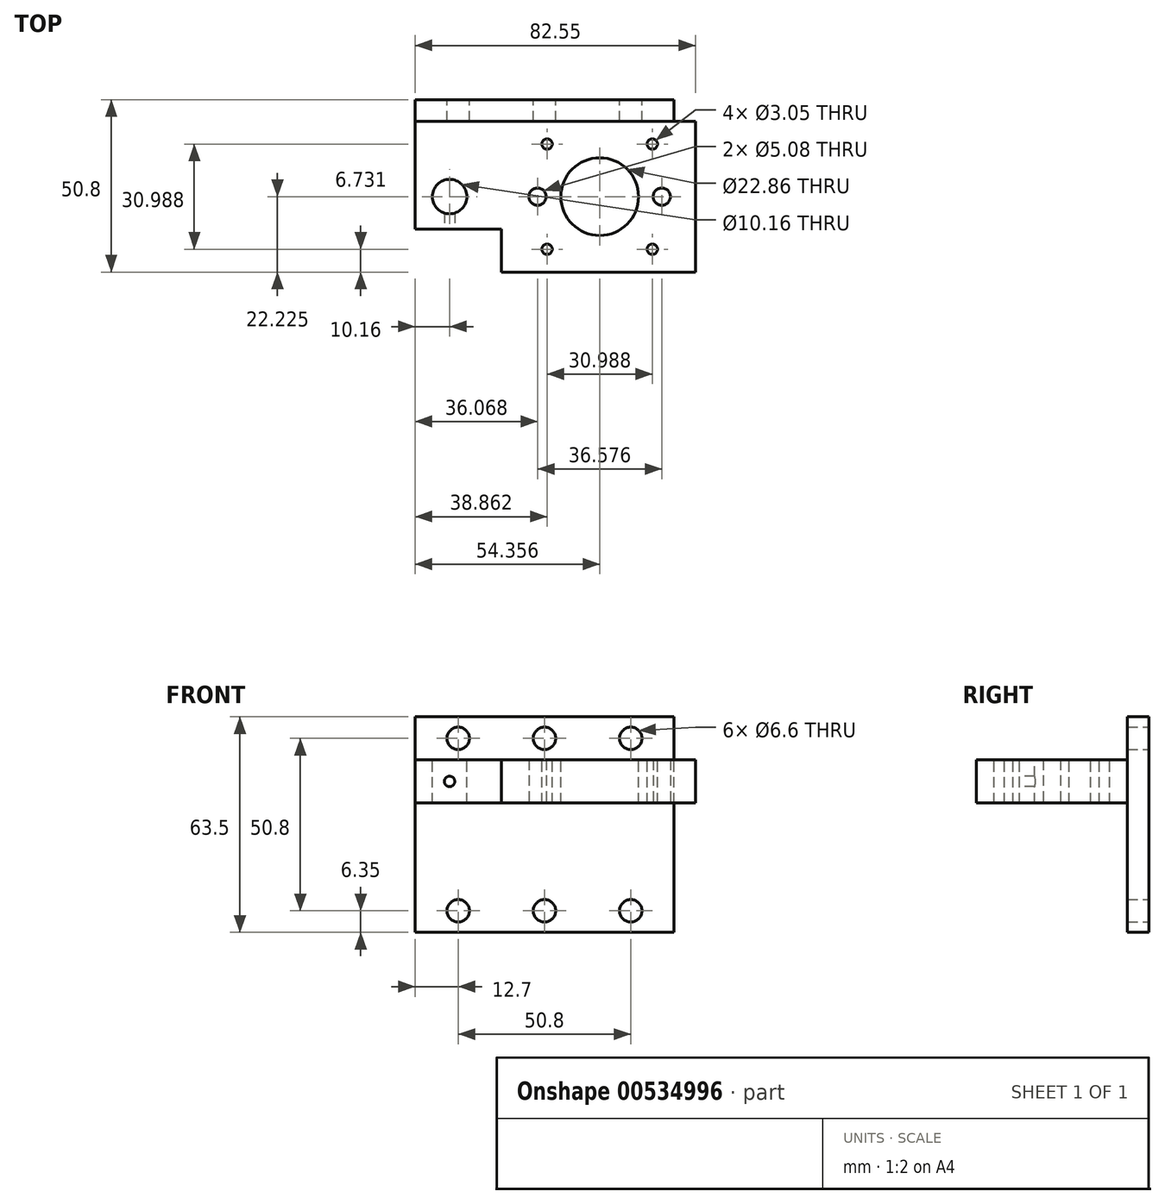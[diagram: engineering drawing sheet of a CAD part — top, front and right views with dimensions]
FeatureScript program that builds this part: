
annotation { "Feature Type Name" : "Feature", "Feature Type Description" : "" }
export const myFeature = defineFeature(function(context is Context, id is Id, definition is map)
    precondition{}
    {
        {
            var Q0;
            Q0=qCreatedBy(makeId("Front.planeOp"),FACE);
            var sketch = newSketch(context, id + "F0", { "sketchPlane" : qUnion([Q0])});
            skLineSegment(sketch, "E0.bottom", {"start": v(0, 0) * mm, "end": v(-76.2, 0) * mm});
            skLineSegment(sketch, "E0.top", {"start": v(0, -38.1) * mm, "end": v(-76.2, -38.1) * mm});
            skLineSegment(sketch, "E0.left", {"start": v(0, 0) * mm, "end": v(0, -38.1) * mm});
            skLineSegment(sketch, "E0.right", {"start": v(-76.2, 0) * mm, "end": v(-76.2, -38.1) * mm});
            skLineSegment(sketch, "E1.0", {"start": v(0, 12.7) * mm, "end": v(-76.2, 12.7) * mm});
            skLineSegment(sketch, "E2.0", {"start": v(0, -50.8) * mm, "end": v(-76.2, -50.8) * mm});
            skLineSegment(sketch, "E3", {"start": v(-76.2, 12.7) * mm, "end": v(-76.2, 0) * mm});
            skLineSegment(sketch, "E4", {"start": v(-76.2, -50.8) * mm, "end": v(-76.2, -38.1) * mm});
            skLineSegment(sketch, "E5", {"start": v(0, -50.8) * mm, "end": v(0, -38.1) * mm});
            skLineSegment(sketch, "E6", {"start": v(0, 0) * mm, "end": v(0, 12.7) * mm});
            skCircle(sketch, "E7", {"center": v(-63.5, 6.35) * mm, "radius": 3.3 * mm});
            skCircle(sketch, "E8", {"center": v(-38.1, 6.35) * mm, "radius": 3.3 * mm});
            skCircle(sketch, "E9", {"center": v(-12.7, 6.35) * mm, "radius": 3.3 * mm});
            skCircle(sketch, "E10", {"center": v(-12.7, -44.45) * mm, "radius": 3.3 * mm});
            skCircle(sketch, "E11", {"center": v(-38.1, -44.45) * mm, "radius": 3.3 * mm});
            skCircle(sketch, "E12", {"center": v(-63.5, -44.45) * mm, "radius": 3.3 * mm});
            skPoint(sketch, "E13.trimOffspring.end.orphan", {"position": v(-76.2, 6.35) * mm});
            skPoint(sketch, "E14.0.start.orphan", {"position": v(0, 6.35) * mm});
            skPoint(sketch, "E15.start.orphan", {"position": v(-63.5, -38.1) * mm});
            skPoint(sketch, "E16.trimOffspring.end.orphan", {"position": v(-63.5, -50.8) * mm});
            skPoint(sketch, "E17.start.orphan", {"position": v(-38.1, -38.1) * mm});
            skPoint(sketch, "E18.trimOffspring.end.orphan", {"position": v(-38.1, -50.8) * mm});
            skPoint(sketch, "E19.start.orphan", {"position": v(-12.7, -38.1) * mm});
            skPoint(sketch, "E20.trimOffspring.end.orphan", {"position": v(-12.7, -50.8) * mm});
            skPoint(sketch, "E21.start.orphan", {"position": v(-12.7, 0) * mm});
            skPoint(sketch, "E22.trimOffspring.end.orphan", {"position": v(-12.7, 12.7) * mm});
            skPoint(sketch, "E23.trimOffspring.end.orphan", {"position": v(-38.1, 12.7) * mm});
            skPoint(sketch, "E24.trimOffspring.end.orphan", {"position": v(-63.5, 12.7) * mm});
            skPoint(sketch, "E25.start.orphan", {"position": v(-63.5, 0) * mm});
            skSolve(sketch);
        }
        {
            var Q0;
            Q0=makeQuery(id+"F0.imprint","IMPRINT",FACE,{"disambiguationData":[TD([[makeQuery(id+"F0.imprint","IMPRINT",EDGE,{"derivedFrom":sQuery(id+"F0.wireOp",EDGE,"E0.bottom")}),-1.0]])]});
            var Q1;
            Q1=makeQuery(id+"F0.imprint","IMPRINT",FACE,{"disambiguationData":[TD([[makeQuery(id+"F0.imprint","IMPRINT",EDGE,{"derivedFrom":sQuery(id+"F0.wireOp",EDGE,"E0.top")}),1.0]])]});
            extrude(context, id + "F1", {"entities" : qUnion([Q0, Q1]), "depth" : 6.35 * mm, "offsetDistance" : 25.4 * mm});
        }
        {
            var Q0;
            Q0=makeQuery(id+"F0.imprint","IMPRINT",FACE,{"disambiguationData":[TD([[makeQuery(id+"F0.imprint","IMPRINT",EDGE,{"derivedFrom":sQuery(id+"F0.wireOp",EDGE,"E0.bottom")}),1.0]])]});
            extrude(context, id + "F2", {"entities" : qUnion([Q0]), "depth" : 50.8 * mm, "offsetDistance" : 25.4 * mm});
        }
        {
            var Q0;
            Q0=makeQuery(id+"F1.opExtrude","SWEPT_BODY",BODY,{"disambiguationData":[OSD([sQuery(id+"F0.wireOp",EDGE,"E0.bottom"),sQuery(id+"F0.wireOp",EDGE,"E1.0"),sQuery(id+"F0.wireOp",EDGE,"E3"),sQuery(id+"F0.wireOp",EDGE,"E6"),sQuery(id+"F0.wireOp",EDGE,"E7"),sQuery(id+"F0.wireOp",EDGE,"E8"),sQuery(id+"F0.wireOp",EDGE,"E9")])]});
            var Q1;
            Q1=makeQuery(id+"F1.opExtrude","SWEPT_BODY",BODY,{"disambiguationData":[OSD([sQuery(id+"F0.wireOp",EDGE,"E0.top"),sQuery(id+"F0.wireOp",EDGE,"E2.0"),sQuery(id+"F0.wireOp",EDGE,"E4"),sQuery(id+"F0.wireOp",EDGE,"E5"),sQuery(id+"F0.wireOp",EDGE,"E10"),sQuery(id+"F0.wireOp",EDGE,"E11"),sQuery(id+"F0.wireOp",EDGE,"E12")])]});
            var Q2;
            Q2=makeQuery(id+"F2.opExtrude","SWEPT_BODY",BODY,{"disambiguationData":[OSD([sQuery(id+"F0.wireOp",EDGE,"E0.bottom"),sQuery(id+"F0.wireOp",EDGE,"E0.top"),sQuery(id+"F0.wireOp",EDGE,"E0.left"),sQuery(id+"F0.wireOp",EDGE,"E0.right")])]});
            booleanBodies(context, id + "F3", {"operationType" : BooleanOperationType.UNION, "tools" : qUnion([Q0, Q1, Q2])});
        }
        {
            var Q0;
            Q0=makeQuery(id+"F2.opExtrude","SWEPT_FACE",FACE,{"disambiguationData":[OSD([sQuery(id+"F0.wireOp",EDGE,"E0.bottom")])]});
            var sketch = newSketch(context, id + "F4", { "sketchPlane" : qUnion([Q0])});
            skCircle(sketch, "E26", {"center": v(-6.35, -44.07) * mm, "radius": 1.52 * mm});
            skCircle(sketch, "E27", {"center": v(-6.35, -13.08) * mm, "radius": 1.52 * mm});
            skCircle(sketch, "E28", {"center": v(-37.34, -13.08) * mm, "radius": 1.52 * mm});
            skCircle(sketch, "E29", {"center": v(-37.34, -44.07) * mm, "radius": 1.52 * mm});
            skCircle(sketch, "E30", {"center": v(-21.84, -28.58) * mm, "radius": 11.43 * mm});
            skPoint(sketch, "E31.start.orphan", {"position": v(-21.84, -44.07) * mm});
            skPoint(sketch, "E32.trimOffspring.end.orphan", {"position": v(-21.84, -13.08) * mm});
            skPoint(sketch, "E33.0.end.orphan", {"position": v(-6.35, -28.58) * mm});
            skPoint(sketch, "E34.trimOffspring.start.orphan", {"position": v(-37.34, -28.58) * mm});
            skPoint(sketch, "E35.orphan", {"position": v(-35.81, -13.08) * mm});
            skPoint(sketch, "E36.trimOffspring.start.orphan", {"position": v(-7.87, -13.08) * mm});
            skPoint(sketch, "E37.orphan", {"position": v(-7.87, -44.07) * mm});
            skPoint(sketch, "E38.trimOffspring.end.orphan", {"position": v(-35.81, -44.07) * mm});
            skCircle(sketch, "E39", {"center": v(-66.04, -28.58) * mm, "radius": 5.08 * mm});
            skPoint(sketch, "E40.trimOffspring.end.orphan", {"position": v(-76.2, -28.58) * mm});
            skPoint(sketch, "E41.0.start.orphan", {"position": v(-66.04, -50.8) * mm});
            skPoint(sketch, "E42.trimOffspring.end.orphan", {"position": v(-66.04, -6.35) * mm});
            skLineSegment(sketch, "E43.bottom", {"start": v(-76.2, -50.8) * mm, "end": v(-50.8, -50.8) * mm});
            skLineSegment(sketch, "E43.top", {"start": v(-76.2, -38.1) * mm, "end": v(-50.8, -38.1) * mm});
            skLineSegment(sketch, "E43.left", {"start": v(-76.2, -50.8) * mm, "end": v(-76.2, -38.1) * mm});
            skLineSegment(sketch, "E43.right", {"start": v(-50.8, -50.8) * mm, "end": v(-50.8, -38.1) * mm});
            skSolve(sketch);
        }
        {
            var Q0;
            Q0 = qSketchRegion(id + "F4", true);
            extrude(context, id + "F5", {"entities" : qUnion([Q0]), "operationType" : NewBodyOperationType.REMOVE, "oppositeDirection" : true, "depth" : 50.8 * mm, "offsetDistance" : 25.4 * mm});
        }
        {
            var Q0;
            Q0=makeQuery(id+"F2.opExtrude","SWEPT_FACE",FACE,{"disambiguationData":[OSD([sQuery(id+"F0.wireOp",EDGE,"E0.top")])]});
            extrude(context, id + "F6", {"entities" : qUnion([Q0]), "operationType" : NewBodyOperationType.REMOVE, "oppositeDirection" : true, "depth" : 25.4 * mm, "offsetDistance" : 25.4 * mm});
        }
        {
            var Q0;
            Q0=makeQuery(id+"F5.boolean.opBoolean","COPY",FACE,{"derivedFrom":makeQuery(id+"F5.opExtrude","SWEPT_FACE",FACE,{"disambiguationData":[OSD([sQuery(id+"F4.wireOp",EDGE,"E43.top")])]})});
            var sketch = newSketch(context, id + "F7", { "sketchPlane" : qUnion([Q0])});
            skLineSegment(sketch, "E44.0", {"start": v(-66.04, -12.7) * mm, "end": v(-66.04, -7.87) * mm});
            skLineSegment(sketch, "E45", {"start": v(-76.2, -6.35) * mm, "end": v(-67.56, -6.35) * mm});
            skCircle(sketch, "E46", {"center": v(-66.04, -6.35) * mm, "radius": 1.52 * mm});
            skLineSegment(sketch, "E47.trimOffspring", {"start": v(-64.52, -6.35) * mm, "end": v(-50.8, -6.35) * mm});
            skLineSegment(sketch, "E48.trimOffspring", {"start": v(-66.04, -4.83) * mm, "end": v(-66.04, 0) * mm});
            skSolve(sketch);
        }
        {
            var Q0;
            Q0 = qSketchRegion(id + "F7", true);
            extrude(context, id + "F8", {"entities" : qUnion([Q0]), "operationType" : NewBodyOperationType.REMOVE, "oppositeDirection" : true, "depth" : 7.62 * mm, "offsetDistance" : 25.4 * mm});
        }
        {
            var Q0;
            Q0=makeQuery(id+"F3.opBoolean","MERGE",FACE,{"derivedFrom":[makeQuery(id+"F1.opExtrude","SWEPT_FACE",FACE,{"disambiguationData":[OSD([sQuery(id+"F0.wireOp",EDGE,"E5")])]}),makeQuery(id+"F1.opExtrude","SWEPT_FACE",FACE,{"disambiguationData":[OSD([sQuery(id+"F0.wireOp",EDGE,"E6")])]}),makeQuery(id+"F2.opExtrude","SWEPT_FACE",FACE,{"disambiguationData":[OSD([sQuery(id+"F0.wireOp",EDGE,"E0.left")])]})]});
            var sketch = newSketch(context, id + "F9", { "sketchPlane" : qUnion([Q0])});
            skLineSegment(sketch, "E49", {"start": v(-6.35, -12.7) * mm, "end": v(-6.35, 0) * mm});
            skSolve(sketch);
        }
        {
            var Q0;
            Q0 = qSketchRegion(id + "F9", true);
            var Q1;
            Q1=makeQuery(id+"F9.imprint","IMPRINT",FACE,{"disambiguationData":[TD([[makeQuery(id+"F9.imprint","IMPRINT",EDGE,{"derivedFrom":sQuery(id+"F9.wireOp",EDGE,"E49")}),1.0]])]});
            extrude(context, id + "F10", {"entities" : qUnion([Q0, Q1]), "operationType" : NewBodyOperationType.ADD, "depth" : 6.35 * mm, "offsetDistance" : 25.4 * mm});
        }
        {
            var Q0;
            {var subQ0=sQuery(id+"F0.wireOp",EDGE,"E0.top");Q0=makeQuery(id+"F10.boolean.opBoolean","MERGE",FACE,{"derivedFrom":[makeQuery(id+"F6.boolean.opBoolean","COPY",FACE,{"derivedFrom":makeQuery(id+"F6.opExtrude","CAP_FACE",FACE,{"disambiguationData":[OSD([subQ0])],"isStart":false})}),makeQuery(id+"F10.opExtrude","SWEPT_FACE",FACE,{"disambiguationData":[OSD([subQ0,sQuery(id+"F0.wireOp",EDGE,"E0.left"),sQuery(id+"F0.wireOp",EDGE,"E5")])]})]});}
            var sketch = newSketch(context, id + "F11", { "sketchPlane" : qUnion([Q0])});
            skLineSegment(sketch, "E50", {"start": v(-21.84, 28.58) * mm, "end": v(-6.1, 28.58) * mm});
            skLineSegment(sketch, "E51", {"start": v(-21.84, 28.58) * mm, "end": v(-37.6, 28.58) * mm});
            skCircle(sketch, "E52", {"center": v(-40.13, 28.58) * mm, "radius": 2.54 * mm});
            skCircle(sketch, "E53", {"center": v(-3.56, 28.58) * mm, "radius": 2.54 * mm});
            skLineSegment(sketch, "E54.trimOffspring", {"start": v(-42.67, 28.58) * mm, "end": v(-45.72, 28.58) * mm});
            skLineSegment(sketch, "E55.trimOffspring", {"start": v(-1.02, 28.58) * mm, "end": v(2.03, 28.58) * mm});
            skSolve(sketch);
        }
        {
            var Q0;
            Q0 = qSketchRegion(id + "F11", true);
            extrude(context, id + "F12", {"entities" : qUnion([Q0]), "operationType" : NewBodyOperationType.REMOVE, "oppositeDirection" : true, "depth" : 25.4 * mm, "offsetDistance" : 25.4 * mm});
        }
    });
